# Revit family: BOS-Umfassungszarge-als-Blockprofil-DIN-18111-1-STW_Familie
name_source: partatom
category: Türen
revit_build: Autodesk Revit 2017 (Build: 20160225_1515(x64)
units: mm (PartAtom-declared; Revit-internal decimal feet)

## family parameters
Basisbauteil = Wand
Beim Laden mit Abzugskörper schneiden = Nein
Gemeinsam genutzt = Nein
Immer vertikal = Ja
Raumberechnungspunkt = Ja

## types (1)
- Bud nach DIN 18111-1
    BBL1 Bandbezugslinie   Hinge Position 1 = 241 mm  [stored 0.790682 ft]
    BE max. = 100 mm  [stored 0.328084 ft]
    Bauelement = BOS Stahlzarge
    Beschreibung = Umfassungszarge als Blockprofil nach DIN 18111-1 für Ständerwerk, gefälzt
    Blechstärke = 1.5 mm  [stored 0.00492126 ft]
    Breite = 0 mm  [stored 0 ft]
    Bud nach DIN 18111-1 = Ja
    Dichtung 1 = Ja
    Dicke = 0 mm  [stored 0 ft]
    Doppelfalz = Nein
    Drehpunkt Warnung sichtbar = Ja
    Drehpunktabstand (FM) horizontal = 19 mm  [stored 0.062336 ft]
    Drehpunktabstand (SP) vertikal = 8.5 mm  [stored 0.0278871 ft]
    Drehpunktreferenz horizontal = 500 mm  [stored 1.64042 ft]
    Einfachfalz = Ja
    Einfügepunkt = 30 mm  [stored 0.0984252 ft]
    Falzaufschlag = 15 mm  [stored 0.0492126 ft]
    Falzaufschlag gesamt = 15 mm  [stored 0.0492126 ft]
    Falztiefe = 28.5 mm  [stored 0.0935039 ft]
    Falztiefe 2 = 25 mm  [stored 0.082021 ft]
    Falztiefe gesamt = 28.5 mm  [stored 0.0935039 ft]
    Funktion = Innen
    Gefälzt = Ja
    Hersteller = BOS GmbH Best Of Steel, Lütkenfelde 4, D-48282 Emsdetten
    Info-Texte sichtbar = Ja
    Information in English = Nein
    Material = grundiert, feuerverzinktes Feinblech nach DIN EN 10143
    Material - Bänder = <Nach Kategorie>
    Material - Dichtung = <Nach Kategorie>
    Material - Drückergarnitur = <Nach Kategorie>
    Material - Türblatt = <Nach Kategorie>
    Material - Zarge = <Nach Kategorie>
    Maßauswahl Hinweis sichtbar = Ja
    Modell = Bud nach DIN 18111-1
    Putzwinkel max. = 28 mm  [stored 0.0918635 ft]
    Putzwinkel min. = 8 mm  [stored 0.0262467 ft]
    Rohbaubreite = 0 mm  [stored 0 ft]
    Rohbauhöhe = 0 mm  [stored 0 ft]
    Sickentiefe = 10 mm  [stored 0.0328084 ft]
    Spiegel hinten max. = 45 mm  [stored 0.147638 ft]
    Spiegel hinten min. = 45 mm  [stored 0.147638 ft]
    Spiegel vorne max. = 30 mm  [stored 0.0984252 ft]
    Spiegel vorne min. = 30 mm  [stored 0.0984252 ft]
    Stumpf = Nein
    Technische Infos rund um die Stahlzarge = www.BestOfSteel.de/tools-downloads/technische-infos-rund-um-die-stahlzarge/
    Typenbild = <Keine Auswahl>
    Türblattabstand 1 = 1.5 mm  [stored 0.00492126 ft]
    Türblattabstand 2 = 4.5 mm  [stored 0.0147638 ft]
    Türblattabstand 3 = 4.5 mm  [stored 0.0147638 ft]
    Türblattabstand links-rechts = 3.5 mm  [stored 0.0114829 ft]
    Türblattabstand oben = 4 mm  [stored 0.0131234 ft]
    Türblattabstand unten = 7 mm  [stored 0.0229659 ft]
    Türblattaufschlag = 13 mm
    Türblattstärke = 40 mm  [stored 0.131234 ft]
    Türblattstärke 1 = 14.5 mm  [stored 0.0475722 ft]
    Türblattstärke 2 = 25.5 mm  [stored 0.0836614 ft]
    Türblattstärke 3 = 0 mm  [stored 0 ft]
    Türblattversatz  horizontal = 9.5 mm  [stored 0.031168 ft]
    Türblattversatz vertikal = -7.5 mm  [stored -0.0246063 ft]
    URL = www.BestOfSteel.de/stahlzargen/zargen-fuer-drehfluegeltueren/zargen-gemaess-din/
    Öffnungswinkel max. = 180.00°
    Öffnungswinkel min. = 0.00°

note: [stored X ft] marks values corroborated as IEEE doubles in the binary element streams (Revit-internal decimal feet)
